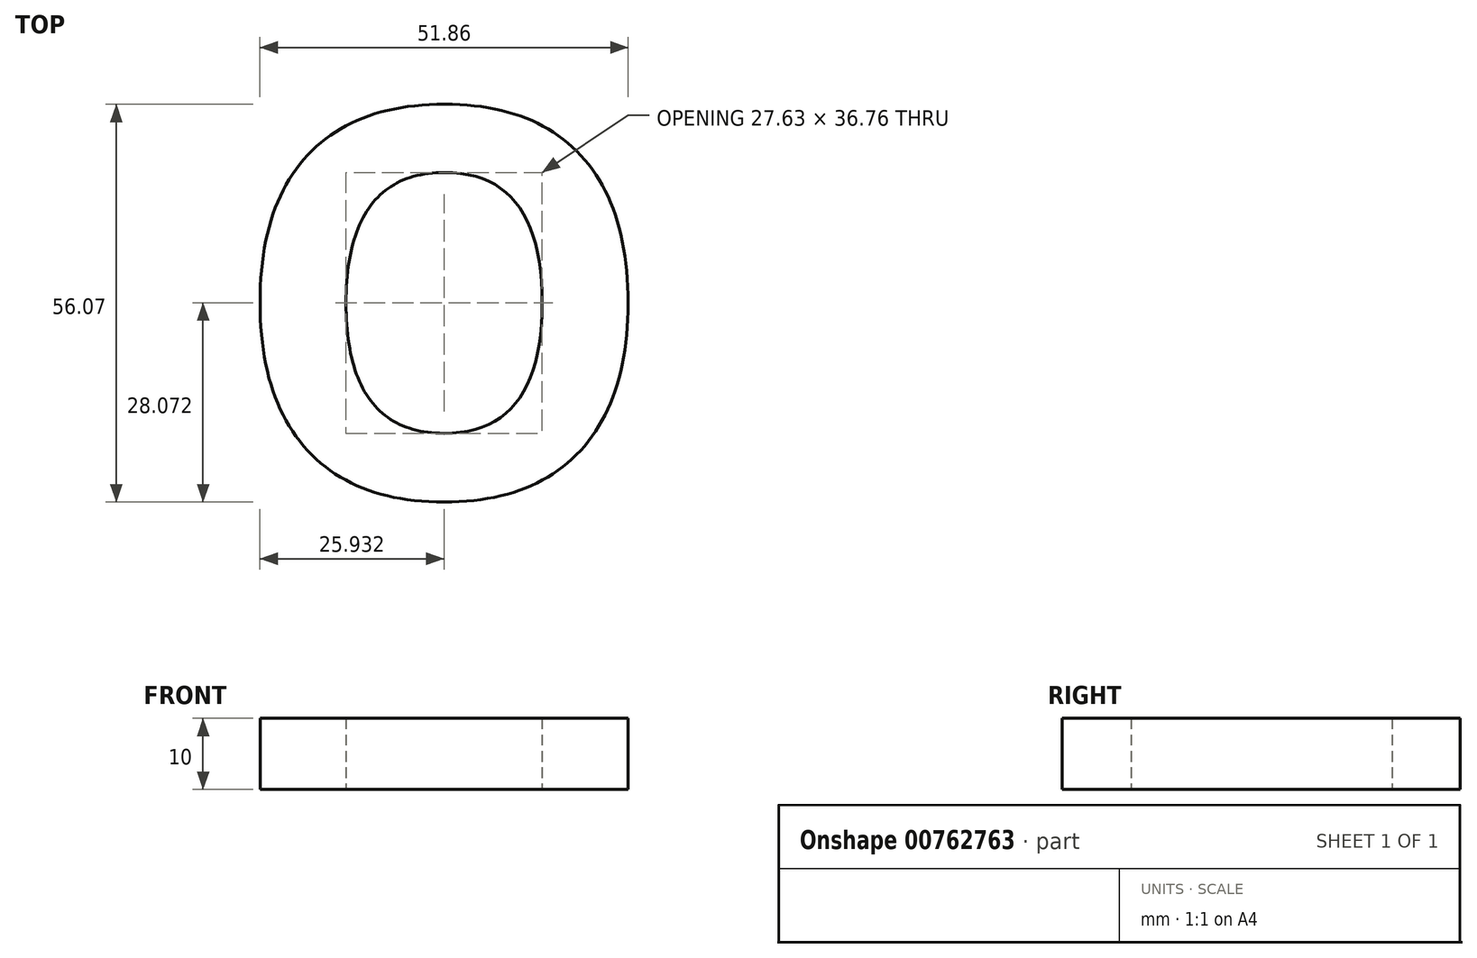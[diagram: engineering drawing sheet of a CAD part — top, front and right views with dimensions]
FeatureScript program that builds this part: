
annotation { "Feature Type Name" : "Feature", "Feature Type Description" : "" }
export const myFeature = defineFeature(function(context is Context, id is Id, definition is map)
    precondition{}
    {
        {
            var Q0;
            Q0=qCreatedBy(makeId("Top.planeOp"),FACE);
            var sketch = newSketch(context, id + "F0", { "sketchPlane" : qUnion([Q0])});
            skText(sketch, "E0", { "text": "O", "fontName": "OpenSans-Bold.ttf"});
            const initialGuessF0  = {"E0": [0, 0, 1, 0, 0.05493]};
            skSetInitialGuess(sketch, initialGuessF0);
            skSolve(sketch);
        }
        {
            var Q0;
            Q0 = qSketchRegion(id + "F0", true);
            extrude(context, id + "F1", {"entities" : qUnion([Q0]), "depth" : 10 * mm, "offsetDistance" : 25 * mm});
        }
    });
